# Revit family: Safa-slat Top Fix
name_source: partatom
category: Generic Models
units: mm (PartAtom-declared; Revit-internal decimal feet)

## family parameters
Always vertical = Yes
Can host rebar = No
Cut with Voids When Loaded = No
Part Type = Normal
Room Calculation Point = No
Round Connector Dimension = Use Diameter
Shared = No
Work Plane-Based = No

## types (5) — shared parameters
Keynote = UNEX SYSTEMS, SAFA-SLAT TOP FIX BALUSTRADE
LENGTH = 2500 mm  [stored 8.2021 ft]
Manufacturer = UNEX SYSTEMS
Max Post Spacing = 1000 mm  [stored 3.28084 ft]
Panel size = 693 mm  [stored 2.27362 ft]
Pannel QTY = 3
Post QTY = 4
Top Rail Height = 24 mm  [stored 0.0787402 ft]
URL = WWW.UNEX.CO.NZ
zero-valued in all types: Default Elevation

## per-type parameters (varying)
| type | ART TOP RAIL | Bal Height | Description | HEIGHT | Model | PPR TOP RAIL | Post Height | VRE TOP RAIL | VRR TOP RAIL | VRT TOP RAIL |
| SAFA-SLAT WITH VRE | No | 1500 mm  [stored 4.92126 ft] | SAFA-SLAT FRAMED BALUSTER WITH VRT TOP RAIL | 1100 mm | SAFA-SLAT RANGE, TOP FIX (VRT) | No | 1076 mm | Yes | No | No |
| SAFA-SLAT WITH PRR | No | 1147 mm | SAFA-SLAT FRAMED BALUSTER WITH PRR TOP RAIL | 1100 mm | SAFA-SLAT RANGE, TOP FIX (PRR) | Yes | 1076 mm | No | No | No |
| SAFA-SLAT WITH ART | Yes | 1147 mm | SAFA-SLAT FRAMED BALUSTER WITH ART TOP RAIL | 1100 mm | SAFA-SLAT RANGE, TOP FIX (ART) | No | 1076 mm | No | No | No |
| SAFA-SLAT WITH VRT | No | 1500 mm  [stored 4.92126 ft] | SAFA-SLAT FRAMED BALUSTER WITH VRT TOP RAIL | 1100 mm | SAFA-SLAT RANGE, TOP FIX (VRT) | No | 1076 mm | No | No | Yes |
| SAFA-SLAT WITH VRR | No | 1147 mm | SAFA-SLAT FRAMED BALUSTER WITH VRR TOP RAIL | 1200 mm | SAFA-SLAT RANGE, TOP FIX (VRR) | No | 1176 mm  [stored 3.85827 ft] | No | Yes | No |

note: [stored X ft] marks values corroborated as IEEE doubles in the binary element streams (Revit-internal decimal feet)

## geometry (parser evidence)
native form markers: Sweep x39
no freeform markers — native parametric forms only
